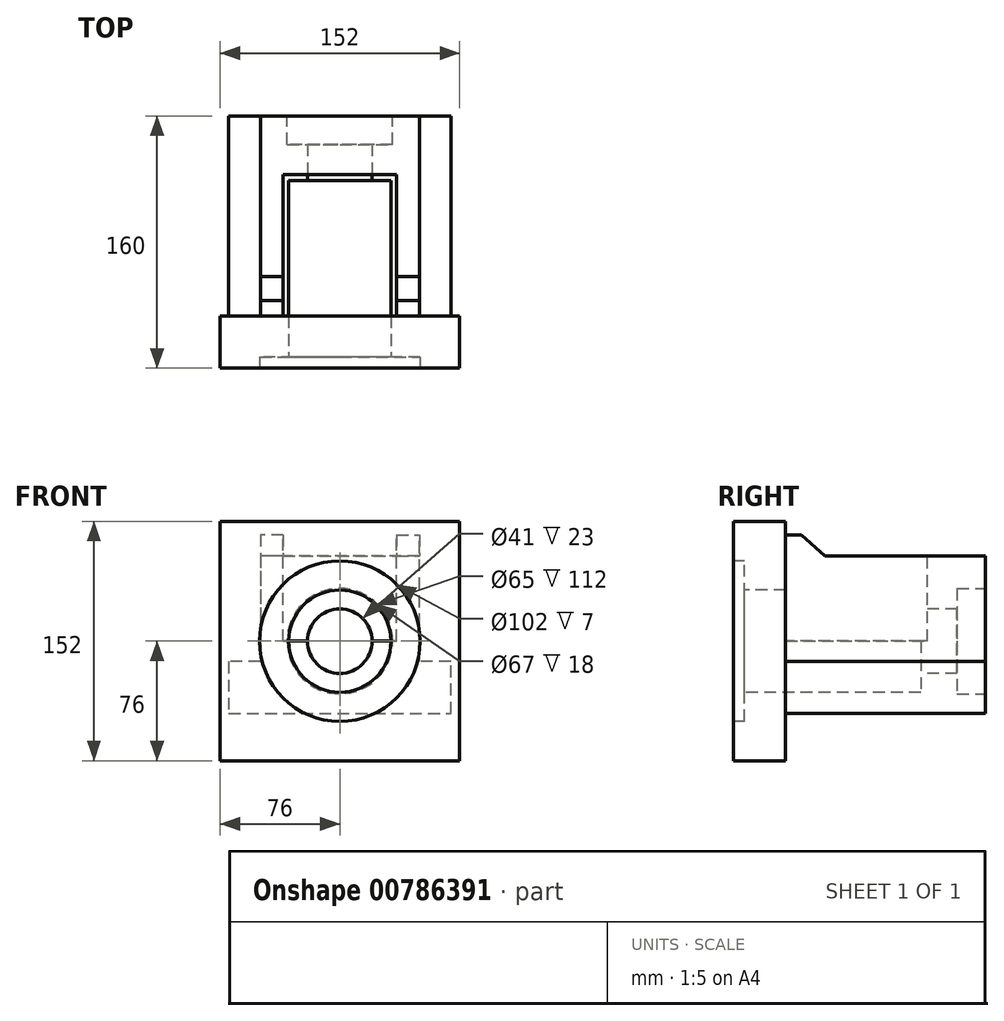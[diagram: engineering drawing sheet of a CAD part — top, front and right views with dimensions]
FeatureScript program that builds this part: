
annotation { "Feature Type Name" : "Feature", "Feature Type Description" : "" }
export const myFeature = defineFeature(function(context is Context, id is Id, definition is map)
    precondition{}
    {
        {
            var Q0;
            Q0=qCreatedBy(makeId("Front.planeOp"),FACE);
            var sketch = newSketch(context, id + "F0", { "sketchPlane" : qUnion([Q0])});
            skLineSegment(sketch, "E0.bottom", {"start": v(76, 76) * mm, "end": v(-76, 76) * mm});
            skLineSegment(sketch, "E0.top", {"start": v(76, -76) * mm, "end": v(-76, -76) * mm});
            skLineSegment(sketch, "E0.left", {"start": v(76, 76) * mm, "end": v(76, -76) * mm});
            skLineSegment(sketch, "E0.right", {"start": v(-76, 76) * mm, "end": v(-76, -76) * mm});
            skPoint(sketch, "E0.middle", {"position": v(0, 0) * mm});
            skSolve(sketch);
        }
        {
            var Q0;
            Q0=qSketchRegion(id+"F0",true);
            extrude(context, id + "F1", {"entities" : qUnion([Q0]), "oppositeDirection" : true, "depth" : 33 * mm, "offsetDistance" : 25 * mm});
        }
        {
            var Q0;
            Q0=makeQuery(id+"F1.opExtrude","CAP_FACE",FACE,{"disambiguationData":[OSD([sQuery(id+"F0.wireOp",EDGE,"E0.bottom"),sQuery(id+"F0.wireOp",EDGE,"E0.top"),sQuery(id+"F0.wireOp",EDGE,"E0.left"),sQuery(id+"F0.wireOp",EDGE,"E0.right")])],"isStart":false});
            var sketch = newSketch(context, id + "F2", { "sketchPlane" : qUnion([Q0])});
            skLineSegment(sketch, "E1", {"start": v(-50.5, 54) * mm, "end": v(50.5, 54) * mm});
            skLineSegment(sketch, "E2", {"start": v(50.5, 54) * mm, "end": v(50.5, -13) * mm});
            skLineSegment(sketch, "E3", {"start": v(50.5, -13) * mm, "end": v(70.5, -13) * mm});
            skLineSegment(sketch, "E4", {"start": v(70.5, -13) * mm, "end": v(70.5, -46) * mm});
            skLineSegment(sketch, "E5", {"start": v(70.5, -46) * mm, "end": v(-70.5, -46) * mm});
            skLineSegment(sketch, "E6", {"start": v(-70.5, -46) * mm, "end": v(-70.5, -13) * mm});
            skLineSegment(sketch, "E7", {"start": v(-70.5, -13) * mm, "end": v(-50.5, -13) * mm});
            skLineSegment(sketch, "E8", {"start": v(-50.5, -13) * mm, "end": v(-50.5, 54) * mm});
            skSolve(sketch);
        }
        {
            var Q0;
            Q0=qSketchRegion(id+"F2",true);
            extrude(context, id + "F3", {"entities" : qUnion([Q0]), "operationType" : NewBodyOperationType.ADD, "depth" : 127 * mm, "offsetDistance" : 25 * mm});
        }
        {
            var Q0;
            Q0=qCreatedBy(makeId("Front.planeOp"),FACE);
            var sketch = newSketch(context, id + "F4", { "sketchPlane" : qUnion([Q0])});
            skCircle(sketch, "E9", {"center": v(0, 0) * mm, "radius": 20.5 * mm});
            skCircle(sketch, "E10", {"center": v(0, 0) * mm, "radius": 32.5 * mm});
            skCircle(sketch, "E11", {"center": v(0, 0) * mm, "radius": 51 * mm});
            skSolve(sketch);
        }
        {
            var Q0;
            Q0=makeQuery(id+"F4.imprint","IMPRINT",FACE,{"disambiguationData":[TD([[makeQuery(id+"F4.imprint","IMPRINT",EDGE,{"derivedFrom":sQuery(id+"F4.wireOp",EDGE,"E9")}),1.0]])]});
            extrude(context, id + "F5", {"entities" : qUnion([Q0]), "operationType" : NewBodyOperationType.REMOVE, "oppositeDirection" : true, "depth" : 156 * mm, "offsetDistance" : 25 * mm});
        }
        {
            var Q0;
            Q0=makeQuery(id+"F4.imprint","IMPRINT",FACE,{"disambiguationData":[TD([[makeQuery(id+"F4.imprint","IMPRINT",EDGE,{"derivedFrom":sQuery(id+"F4.wireOp",EDGE,"E9")}),-1.0]])]});
            var Q1;
            Q1=makeQuery(id+"F4.imprint","IMPRINT",FACE,{"disambiguationData":[TD([[makeQuery(id+"F4.imprint","IMPRINT",EDGE,{"derivedFrom":sQuery(id+"F4.wireOp",EDGE,"E9")}),1.0]])]});
            extrude(context, id + "F6", {"entities" : qUnion([Q0, Q1]), "operationType" : NewBodyOperationType.REMOVE, "oppositeDirection" : true, "depth" : 119 * mm, "offsetDistance" : 25 * mm});
        }
        {
            var Q0;
            Q0=qSketchRegion(id+"F4",true);
            var Q1;
            Q1=makeQuery(id+"F4.imprint","IMPRINT",FACE,{"disambiguationData":[TD([[makeQuery(id+"F4.imprint","IMPRINT",EDGE,{"derivedFrom":sQuery(id+"F4.wireOp",EDGE,"E10")}),-1.0]])]});
            extrude(context, id + "F7", {"entities" : qUnion([Q0, Q1]), "operationType" : NewBodyOperationType.REMOVE, "oppositeDirection" : true, "depth" : 7 * mm, "offsetDistance" : 25 * mm});
        }
        {
            var Q0;
            Q0=makeQuery(id+"F3.opExtrude","CAP_FACE",FACE,{"disambiguationData":[OSD([sQuery(id+"F2.wireOp",EDGE,"E1"),sQuery(id+"F2.wireOp",EDGE,"E2"),sQuery(id+"F2.wireOp",EDGE,"E3"),sQuery(id+"F2.wireOp",EDGE,"E4"),sQuery(id+"F2.wireOp",EDGE,"E5"),sQuery(id+"F2.wireOp",EDGE,"E6"),sQuery(id+"F2.wireOp",EDGE,"E7"),sQuery(id+"F2.wireOp",EDGE,"E8")])],"isStart":false});
            var sketch = newSketch(context, id + "F8", { "sketchPlane" : qUnion([Q0])});
            skCircle(sketch, "E12", {"center": v(0, 0) * mm, "radius": 33.5 * mm});
            skSolve(sketch);
        }
        {
            var Q0;
            Q0=qSketchRegion(id+"F8",true);
            extrude(context, id + "F9", {"entities" : qUnion([Q0]), "operationType" : NewBodyOperationType.REMOVE, "oppositeDirection" : true, "depth" : 18 * mm, "offsetDistance" : 25 * mm});
        }
        {
            var Q0;
            Q0=makeQuery(id+"F3.opExtrude","SWEPT_FACE",FACE,{"disambiguationData":[OSD([sQuery(id+"F2.wireOp",EDGE,"E1")])]});
            var sketch = newSketch(context, id + "F10", { "sketchPlane" : qUnion([Q0])});
            skLineSegment(sketch, "E13.bottom", {"start": v(-36, 33) * mm, "end": v(36, 33) * mm});
            skLineSegment(sketch, "E13.top", {"start": v(-36, 123) * mm, "end": v(36, 123) * mm});
            skLineSegment(sketch, "E13.left", {"start": v(-36, 33) * mm, "end": v(-36, 123) * mm});
            skLineSegment(sketch, "E13.right", {"start": v(36, 33) * mm, "end": v(36, 123) * mm});
            skSolve(sketch);
        }
        {
            var Q0;
            Q0=qSketchRegion(id+"F10",true);
            extrude(context, id + "F11", {"entities" : qUnion([Q0]), "operationType" : NewBodyOperationType.REMOVE, "oppositeDirection" : true, "depth" : 54 * mm, "offsetDistance" : 25 * mm});
        }
        {
            var Q0;
            Q0=makeQuery(id+"F3.opExtrude","SWEPT_FACE",FACE,{"disambiguationData":[OSD([sQuery(id+"F2.wireOp",EDGE,"E8")])]});
            var sketch = newSketch(context, id + "F12", { "sketchPlane" : qUnion([Q0])});
            skLineSegment(sketch, "E14", {"start": v(33, 54) * mm, "end": v(33, 67.5) * mm});
            skLineSegment(sketch, "E15", {"start": v(33, 67.5) * mm, "end": v(43, 67.5) * mm});
            skLineSegment(sketch, "E16", {"start": v(43, 67.5) * mm, "end": v(58, 54) * mm});
            skLineSegment(sketch, "E17", {"start": v(58, 54) * mm, "end": v(33, 54) * mm});
            skSolve(sketch);
        }
        {
            var Q0;
            Q0=qSketchRegion(id+"F12",true);
            extrude(context, id + "F13", {"entities" : qUnion([Q0]), "operationType" : NewBodyOperationType.ADD, "oppositeDirection" : true, "depth" : 14.5 * mm, "offsetDistance" : 25 * mm});
        }
        {
            var Q0;
            Q0=makeQuery(id+"F3.opExtrude","SWEPT_FACE",FACE,{"disambiguationData":[OSD([sQuery(id+"F2.wireOp",EDGE,"E2")])]});
            var sketch = newSketch(context, id + "F14", { "sketchPlane" : qUnion([Q0])});
            skLineSegment(sketch, "E18", {"start": v(-33, 54) * mm, "end": v(-33, 67.5) * mm});
            skLineSegment(sketch, "E19", {"start": v(-33, 67.5) * mm, "end": v(-43, 67.5) * mm});
            skLineSegment(sketch, "E20", {"start": v(-43, 67.5) * mm, "end": v(-58, 54) * mm});
            skLineSegment(sketch, "E21", {"start": v(-58, 54) * mm, "end": v(-33, 54) * mm});
            skSolve(sketch);
        }
        {
            var Q0;
            Q0=qSketchRegion(id+"F14",true);
            extrude(context, id + "F15", {"entities" : qUnion([Q0]), "operationType" : NewBodyOperationType.ADD, "oppositeDirection" : true, "depth" : 14.5 * mm, "offsetDistance" : 25 * mm});
        }
    });
